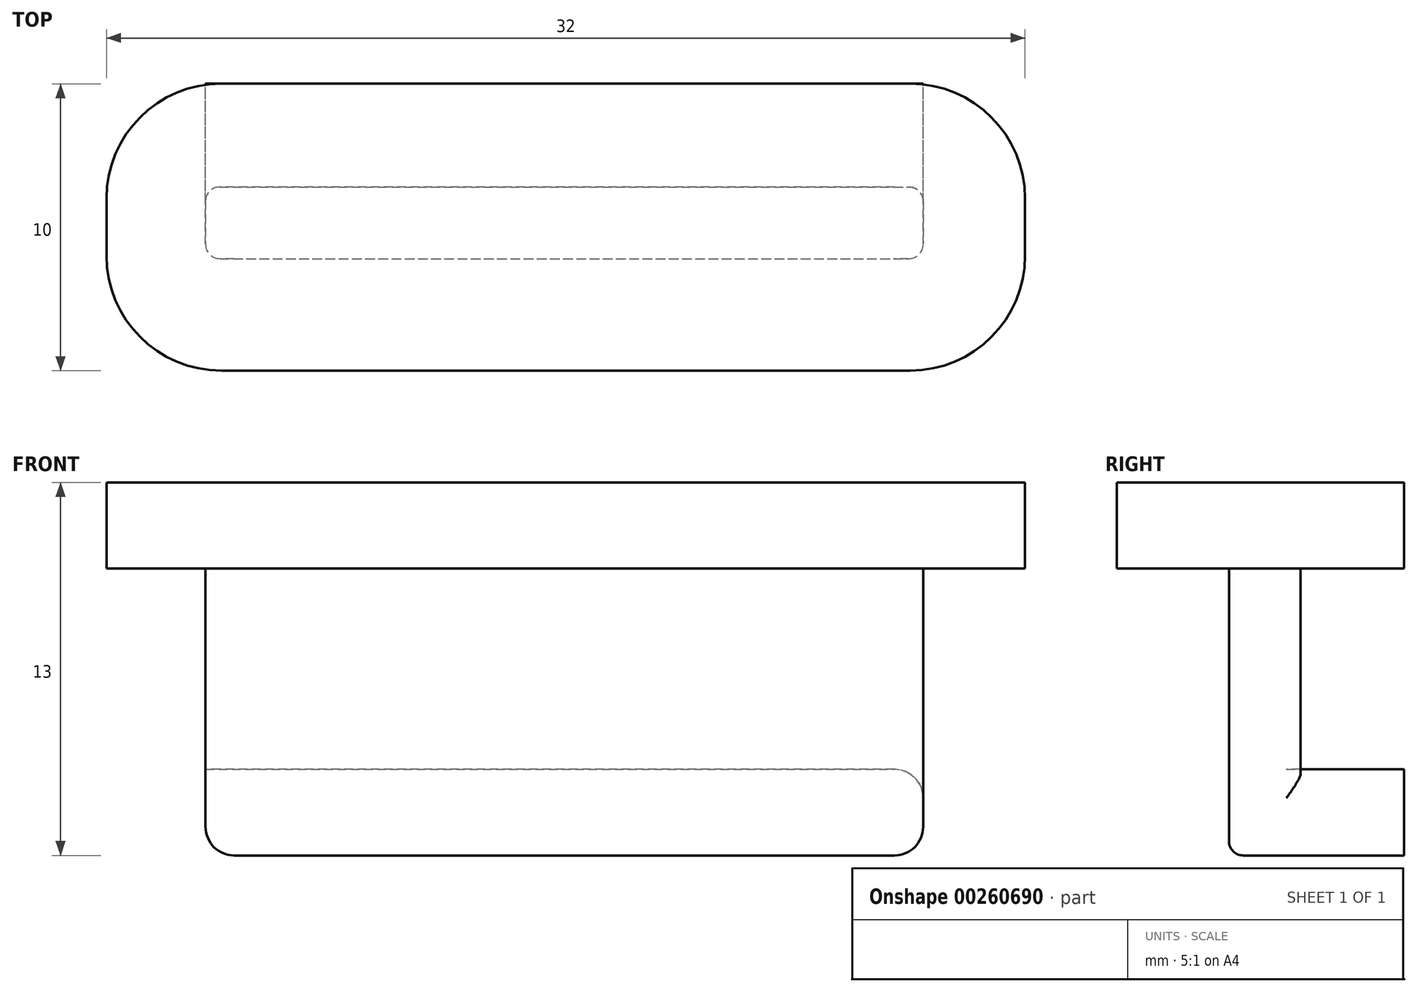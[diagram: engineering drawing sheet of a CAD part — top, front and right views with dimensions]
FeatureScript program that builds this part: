
annotation { "Feature Type Name" : "Feature", "Feature Type Description" : "" }
export const myFeature = defineFeature(function(context is Context, id is Id, definition is map)
    precondition{}
    {
        {
            var Q0;
            Q0=qCreatedBy(makeId("Top.planeOp"),FACE);
            var sketch = newSketch(context, id + "F0", { "sketchPlane" : qUnion([Q0])});
            skLineSegment(sketch, "E0.bottom", {"start": v(-12.02, 1.17) * mm, "end": v(12.98, 1.17) * mm});
            skLineSegment(sketch, "E0.top", {"start": v(-12.02, -1.33) * mm, "end": v(12.98, -1.33) * mm});
            skLineSegment(sketch, "E0.left", {"start": v(-12.02, 1.17) * mm, "end": v(-12.02, -1.33) * mm});
            skLineSegment(sketch, "E0.right", {"start": v(12.98, 1.17) * mm, "end": v(12.98, -1.33) * mm});
            skLineSegment(sketch, "E1.bottom", {"start": v(-15.47, 4.77) * mm, "end": v(16.53, 4.77) * mm});
            skLineSegment(sketch, "E1.top", {"start": v(-15.47, -5.23) * mm, "end": v(16.53, -5.23) * mm});
            skLineSegment(sketch, "E1.left", {"start": v(-15.47, 4.77) * mm, "end": v(-15.47, -5.23) * mm});
            skLineSegment(sketch, "E1.right", {"start": v(16.53, 4.77) * mm, "end": v(16.53, -5.23) * mm});
            skLineSegment(sketch, "E2", {"start": v(-12.02, 1.17) * mm, "end": v(-12.02, 31.22) * mm});
            skLineSegment(sketch, "E3", {"start": v(12.98, 1.17) * mm, "end": v(12.98, 9.87) * mm});
            skArc(sketch, "E4", {"start": v(-12.02, 31.22) * mm, "mid": v(-0.92, 44.85) * mm, "end": v(14.69, 36.75) * mm});
            skArc(sketch, "E5", {"start": v(12.98, 9.87) * mm, "mid": v(9.2, 19.23) * mm, "end": v(0, 23.37) * mm});
            skArc(sketch, "E6", {"start": v(14.69, 36.75) * mm, "mid": v(13.08, 32.13) * mm, "end": v(8.34, 33.33) * mm});
            skArc(sketch, "E7", {"start": v(8.34, 33.33) * mm, "mid": v(-2.52, 33.96) * mm, "end": v(0, 23.37) * mm});
            skSolve(sketch);
        }
        {
            var Q0;
            {var subQ0=sQuery(id+"F0.wireOp",EDGE,"E4");Q0=makeQuery(id+"F0.imprint","IMPRINT",FACE,{"disambiguationData":[TD([[makeQuery(id+"F0.imprint","IMPRINT",EDGE,{"derivedFrom":subQ0}),-1.0]])]});}
            var Q1;
            {var subQ0=sQuery(id+"F0.wireOp",EDGE,"E0.bottom");Q1=makeQuery(id+"F0.imprint","IMPRINT",FACE,{"disambiguationData":[TD([[makeQuery(id+"F0.imprint","IMPRINT",EDGE,{"derivedFrom":subQ0}),1.0]])]});}
            var Q2;
            Q2=makeQuery(id+"F0.imprint","IMPRINT",FACE,{"disambiguationData":[TD([[makeQuery(id+"F0.imprint","IMPRINT",EDGE,{"derivedFrom":sQuery(id+"F0.wireOp",EDGE,"E0.bottom")}),-1.0]])]});
            extrude(context, id + "F1", {"entities" : qUnion([Q0, Q1, Q2]), "depth" : 3 * mm});
        }
        {
            var Q0;
            Q0=makeQuery(id+"F0.imprint","IMPRINT",FACE,{"disambiguationData":[TD([[makeQuery(id+"F0.imprint","IMPRINT",EDGE,{"derivedFrom":sQuery(id+"F0.wireOp",EDGE,"E0.bottom")}),-1.0]])]});
            extrude(context, id + "F2", {"entities" : qUnion([Q0]), "operationType" : NewBodyOperationType.ADD, "depth" : 10 * mm});
        }
        {
            var Q0;
            {var subQ0=sQuery(id+"F0.wireOp",EDGE,"E0.bottom");Q0=makeQuery(id+"F0.imprint","IMPRINT",FACE,{"disambiguationData":[TD([[makeQuery(id+"F0.imprint","IMPRINT",EDGE,{"derivedFrom":subQ0}),1.0]])]});}
            var Q1;
            Q1=makeQuery(id+"F0.imprint","IMPRINT",FACE,{"disambiguationData":[TD([[makeQuery(id+"F0.imprint","IMPRINT",EDGE,{"derivedFrom":sQuery(id+"F0.wireOp",EDGE,"E0.top")}),-1.0]])]});
            var Q2;
            Q2=makeQuery(id+"F0.imprint","IMPRINT",FACE,{"disambiguationData":[TD([[makeQuery(id+"F0.imprint","IMPRINT",EDGE,{"derivedFrom":sQuery(id+"F0.wireOp",EDGE,"E0.bottom")}),-1.0]])]});
            extrude(context, id + "F3", {"entities" : qUnion([Q0, Q1, Q2]), "operationType" : NewBodyOperationType.ADD, "depth" : 13 * mm, "hasSecondDirection" : true, "secondDirectionOppositeDirection" : false, "secondDirectionDepth" : 10 * mm});
        }
        {
            var Q0;
            Q0=makeQuery(id+"F3.opExtrude","SWEPT_EDGE",EDGE,{"disambiguationData":[OSD([sQuery(id+"F0.wireOp",EDGE,"E1.top"),sQuery(id+"F0.wireOp",EDGE,"E1.right")])]});
            var Q1;
            Q1=makeQuery(id+"F3.opExtrude","SWEPT_EDGE",EDGE,{"disambiguationData":[OSD([sQuery(id+"F0.wireOp",EDGE,"E1.bottom"),sQuery(id+"F0.wireOp",EDGE,"E1.right")])]});
            var Q2;
            Q2=makeQuery(id+"F3.opExtrude","SWEPT_EDGE",EDGE,{"disambiguationData":[OSD([sQuery(id+"F0.wireOp",EDGE,"E1.top"),sQuery(id+"F0.wireOp",EDGE,"E1.left")])]});
            var Q3;
            Q3=makeQuery(id+"F3.opExtrude","SWEPT_EDGE",EDGE,{"disambiguationData":[OSD([sQuery(id+"F0.wireOp",EDGE,"E1.bottom"),sQuery(id+"F0.wireOp",EDGE,"E1.left")])]});
            fillet(context, id + "F4", {"entities" : qUnion([Q0, Q1, Q2, Q3]), "radius" : 4 * mm, "tangentPropagation" : true, "allowEdgeOverflow" : false});
        }
        {
            var Q0;
            Q0=makeQuery(id+"F1.opExtrude","CAP_EDGE",EDGE,{"disambiguationData":[OSD([sQuery(id+"F0.wireOp",EDGE,"E7")])],"isStart":false});
            var Q1;
            Q1=makeQuery(id+"F1.opExtrude","CAP_EDGE",EDGE,{"disambiguationData":[OSD([sQuery(id+"F0.wireOp",EDGE,"E5")])],"isStart":false});
            var Q2;
            Q2=makeQuery(id+"F1.opExtrude","CAP_EDGE",EDGE,{"disambiguationData":[OSD([sQuery(id+"F0.wireOp",EDGE,"E0.right"),sQuery(id+"F0.wireOp",EDGE,"E3")])],"isStart":false});
            var Q3;
            Q3=makeQuery(id+"F1.opExtrude","CAP_EDGE",EDGE,{"disambiguationData":[OSD([sQuery(id+"F0.wireOp",EDGE,"E4")])],"isStart":true});
            var Q4;
            Q4=makeQuery(id+"F1.opExtrude","CAP_EDGE",EDGE,{"disambiguationData":[OSD([sQuery(id+"F0.wireOp",EDGE,"E6")])],"isStart":true});
            var Q5;
            Q5=makeQuery(id+"F1.opExtrude","CAP_EDGE",EDGE,{"disambiguationData":[OSD([sQuery(id+"F0.wireOp",EDGE,"E7")])],"isStart":true});
            var Q6;
            Q6=makeQuery(id+"F1.opExtrude","CAP_EDGE",EDGE,{"disambiguationData":[OSD([sQuery(id+"F0.wireOp",EDGE,"E5")])],"isStart":true});
            var Q7;
            Q7=makeQuery(id+"F1.opExtrude","CAP_EDGE",EDGE,{"disambiguationData":[OSD([sQuery(id+"F0.wireOp",EDGE,"E0.right"),sQuery(id+"F0.wireOp",EDGE,"E3")])],"isStart":true});
            var Q8;
            Q8=makeQuery(id+"F1.opExtrude","CAP_EDGE",EDGE,{"disambiguationData":[OSD([sQuery(id+"F0.wireOp",EDGE,"E0.left"),sQuery(id+"F0.wireOp",EDGE,"E2")])],"isStart":true});
            var Q9;
            Q9=makeQuery(id+"F1.opExtrude","CAP_EDGE",EDGE,{"disambiguationData":[OSD([sQuery(id+"F0.wireOp",EDGE,"E5")])],"isStart":true});
            var Q10;
            Q10=makeQuery(id+"F1.opExtrude","CAP_EDGE",EDGE,{"disambiguationData":[OSD([sQuery(id+"F0.wireOp",EDGE,"E0.right"),sQuery(id+"F0.wireOp",EDGE,"E3")])],"isStart":true});
            fillet(context, id + "F5", {"entities" : qUnion([Q0, Q1, Q2, Q3, Q4, Q5, Q6, Q7, Q8, Q9, Q10]), "radius" : 1 * mm, "tangentPropagation" : true, "allowEdgeOverflow" : false});
        }
        {
            var Q0;
            Q0=makeQuery(id+"F2.opExtrude","SWEPT_EDGE",EDGE,{"disambiguationData":[OSD([sQuery(id+"F0.wireOp",EDGE,"E0.bottom"),sQuery(id+"F0.wireOp",EDGE,"E0.right"),sQuery(id+"F0.wireOp",EDGE,"E3")])]});
            var Q1;
            Q1=makeQuery(id+"F2.opExtrude","SWEPT_EDGE",EDGE,{"disambiguationData":[OSD([sQuery(id+"F0.wireOp",EDGE,"E0.bottom"),sQuery(id+"F0.wireOp",EDGE,"E0.left"),sQuery(id+"F0.wireOp",EDGE,"E2")])]});
            var Q2;
            {var subQ0=sQuery(id+"F0.wireOp",EDGE,"E0.left");var subQ1=sQuery(id+"F0.wireOp",EDGE,"E0.top");Q2=makeQuery(id+"F2.boolean.opBoolean","MERGE",EDGE,{"derivedFrom":[makeQuery(id+"F1.opExtrude","SWEPT_EDGE",EDGE,{"disambiguationData":[OSD([subQ1,subQ0])]}),makeQuery(id+"F2.opExtrude","SWEPT_EDGE",EDGE,{"disambiguationData":[OSD([subQ1,subQ0])]})]});}
            fillet(context, id + "F6", {"entities" : qUnion([Q0, Q1, Q2]), "radius" : .5 * mm, "tangentPropagation" : true, "allowEdgeOverflow" : false});
        }
    });
